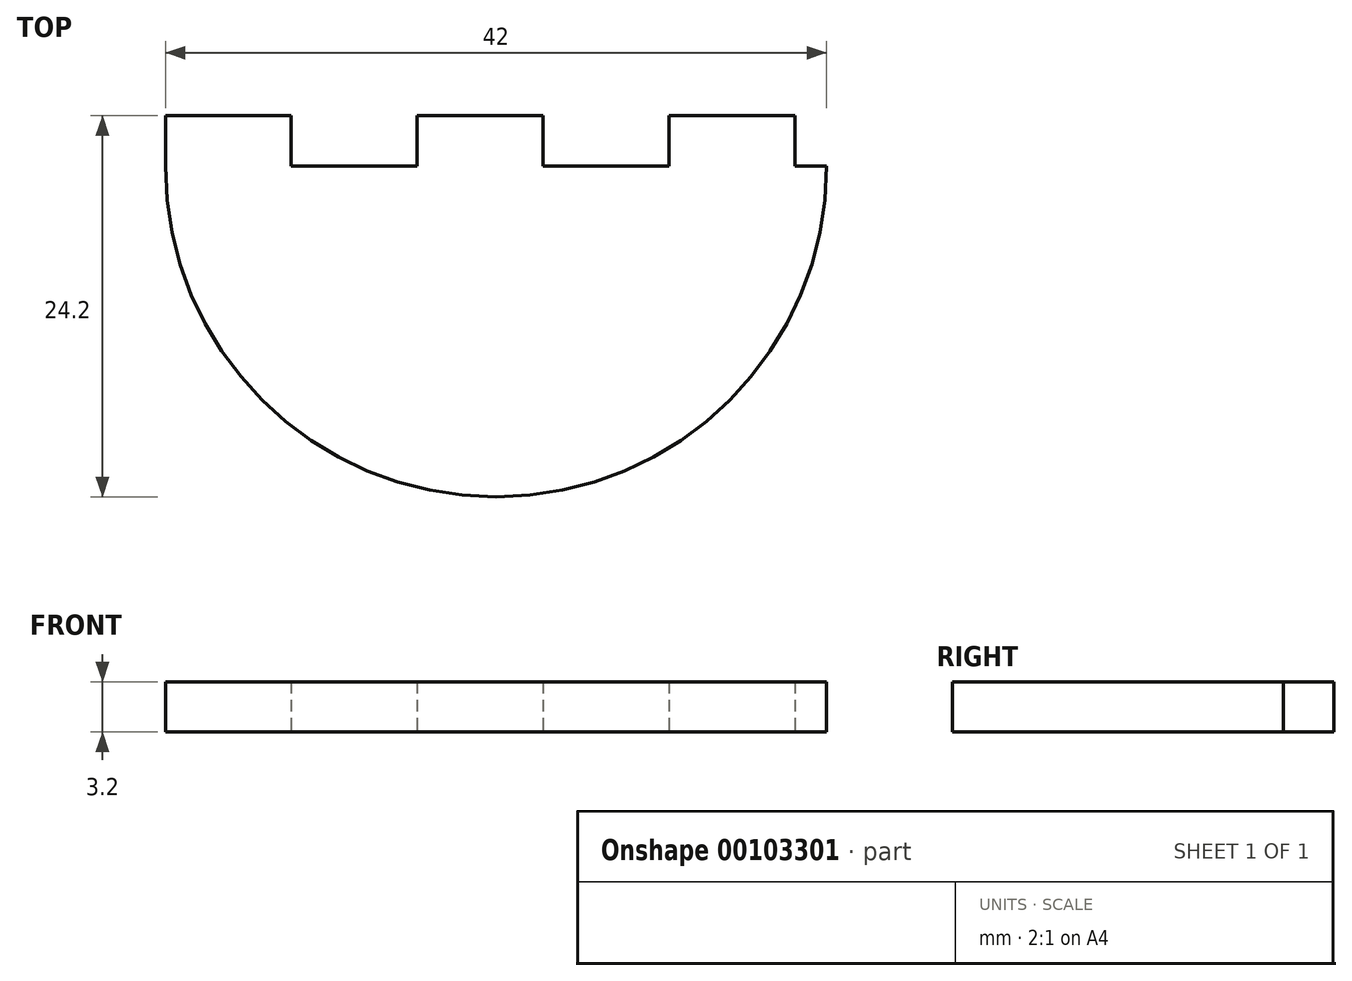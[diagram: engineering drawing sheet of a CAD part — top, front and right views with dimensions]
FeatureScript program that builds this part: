
annotation { "Feature Type Name" : "Feature", "Feature Type Description" : "" }
export const myFeature = defineFeature(function(context is Context, id is Id, definition is map)
    precondition{}
    {
        {
            var Q0;
            Q0=qCreatedBy(makeId("Top.planeOp"),FACE);
            var sketch = newSketch(context, id + "F0", { "sketchPlane" : qUnion([Q0])});
            skArc(sketch, "E0", {"start": v(-21, 0) * mm, "mid": v(0, -21) * mm, "end": v(21, 0) * mm});
            skLineSegment(sketch, "E1", {"start": v(-21, 0) * mm, "end": v(-21, 3.2) * mm});
            skLineSegment(sketch, "E2", {"start": v(-21, 3.2) * mm, "end": v(-13, 3.2) * mm});
            skLineSegment(sketch, "E3", {"start": v(-13, 3.2) * mm, "end": v(-13, 0) * mm});
            skLineSegment(sketch, "E4", {"start": v(-13, 0) * mm, "end": v(-5, 0) * mm});
            skLineSegment(sketch, "E5", {"start": v(-5, 0) * mm, "end": v(-5, 3.2) * mm});
            skLineSegment(sketch, "E6", {"start": v(-5, 3.2) * mm, "end": v(3, 3.2) * mm});
            skLineSegment(sketch, "E7", {"start": v(3, 3.2) * mm, "end": v(3, 0) * mm});
            skLineSegment(sketch, "E8", {"start": v(3, 0) * mm, "end": v(11, 0) * mm});
            skLineSegment(sketch, "E9", {"start": v(11, 0) * mm, "end": v(11, 3.2) * mm});
            skLineSegment(sketch, "E10", {"start": v(11, 3.2) * mm, "end": v(19, 3.2) * mm});
            skLineSegment(sketch, "E11", {"start": v(19, 3.2) * mm, "end": v(19, 0) * mm});
            skLineSegment(sketch, "E12", {"start": v(19, 0) * mm, "end": v(21, 0) * mm});
            skLineSegment(sketch, "E13", {"start": v(0, 0) * mm, "end": v(0, -21) * mm, "construction": true});
            skLineSegment(sketch, "E14", {"start": v(0, -21) * mm, "end": v(0, -11.5) * mm, "construction": true});
            skSolve(sketch);
        }
        {
            var Q0;
            Q0=makeQuery(id+"F0.imprint","IMPRINT",FACE,{"disambiguationData":[TD([[makeQuery(id+"F0.imprint","IMPRINT",EDGE,{"derivedFrom":sQuery(id+"F0.wireOp",EDGE,"WeAqzrae-46Nc-yjBp-5vXX-3ru7yos8T8HK")}),1.0]])]});
            var Q1;
            Q1=makeQuery(id+"F0.imprint","IMPRINT",FACE,{"disambiguationData":[TD([[makeQuery(id+"F0.imprint","IMPRINT",EDGE,{"derivedFrom":sQuery(id+"F0.wireOp",EDGE,"E0")}),1.0]])]});
            extrude(context, id + "F1", {"entities" : qUnion([Q0, Q1]), "endBound" : BoundingType.SYMMETRIC, "depth" : 3.2 * mm});
        }
    });
